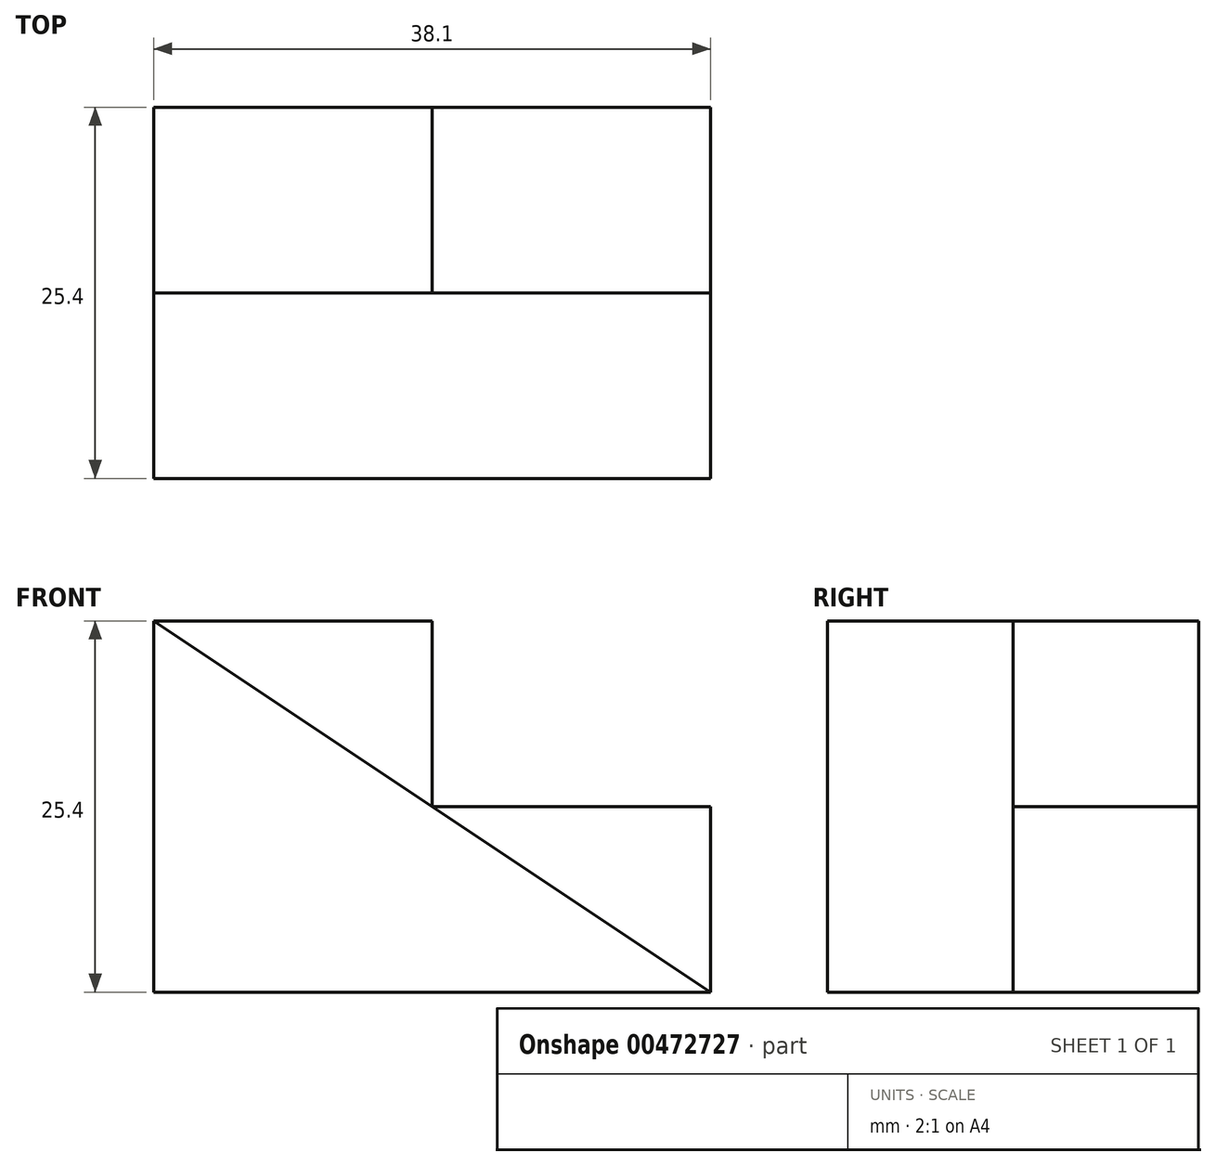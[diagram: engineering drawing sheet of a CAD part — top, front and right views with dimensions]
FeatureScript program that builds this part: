
annotation { "Feature Type Name" : "Feature", "Feature Type Description" : "" }
export const myFeature = defineFeature(function(context is Context, id is Id, definition is map)
    precondition{}
    {
        {
            var Q0;
            Q0=qCreatedBy(makeId("Front.planeOp"),FACE);
            var sketch = newSketch(context, id + "F0", { "sketchPlane" : qUnion([Q0])});
            skLineSegment(sketch, "E0", {"start": v(-6.27, 5.23) * mm, "end": v(-6.27, -20.17) * mm});
            skLineSegment(sketch, "E1", {"start": v(-6.27, -20.17) * mm, "end": v(31.83, -20.17) * mm});
            skLineSegment(sketch, "E2", {"start": v(31.83, -20.17) * mm, "end": v(-6.27, 5.23) * mm});
            skLineSegment(sketch, "E3", {"start": v(-6.27, 5.23) * mm, "end": v(12.78, 5.23) * mm});
            skLineSegment(sketch, "E4", {"start": v(12.78, 5.23) * mm, "end": v(12.78, -7.47) * mm});
            skLineSegment(sketch, "E5", {"start": v(12.78, -7.47) * mm, "end": v(31.83, -7.47) * mm});
            skLineSegment(sketch, "E6", {"start": v(31.83, -7.47) * mm, "end": v(31.83, -20.17) * mm});
            skSolve(sketch);
        }
        {
            var Q0;
            {var subQ0=sQuery(id+"F0.wireOp",EDGE,"E0");Q0=makeQuery(id+"F0.imprint","IMPRINT",FACE,{"disambiguationData":[TD([[makeQuery(id+"F0.imprint","IMPRINT",EDGE,{"derivedFrom":subQ0}),1.0]])]});}
            extrude(context, id + "F1", {"entities" : qUnion([Q0]), "depth" : 25.4 * mm});
        }
        {
            var Q0;
            {var subQ0=sQuery(id+"F0.wireOp",EDGE,"E3");Q0=makeQuery(id+"F0.imprint","IMPRINT",FACE,{"disambiguationData":[TD([[makeQuery(id+"F0.imprint","IMPRINT",EDGE,{"derivedFrom":subQ0}),-1.0]])]});}
            var Q1;
            {var subQ2=sQuery(id+"F0.wireOp",EDGE,"E5");Q1=makeQuery(id+"F0.imprint","IMPRINT",FACE,{"disambiguationData":[TD([[makeQuery(id+"F0.imprint","IMPRINT",EDGE,{"derivedFrom":subQ2}),-1.0]])]});}
            extrude(context, id + "F2", {"entities" : qUnion([Q0, Q1]), "operationType" : NewBodyOperationType.ADD, "depth" : 12.7 * mm});
        }
    });
